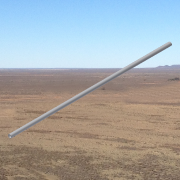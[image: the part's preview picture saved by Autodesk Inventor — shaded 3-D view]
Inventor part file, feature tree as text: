
AUTODESK INVENTOR PART (.ipt)
format: ipt  version: 2013 SP2 (Build 170200200, 200)  size: 123,392 bytes
history: native  units: in
note: dims shown in document units (in); Inventor stores cm internally (conversion verified against a paired STEP export)
features: extrude x1, sketch x1
ambient origin geometry x8: Origin, YZ Plane, XZ Plane, XY Plane, X Axis, Y Axis, Z Axis, Center Point
bodies: Solid1 (feature_tree)
feature tree (2):
  extrude  "Extrusion1"  Depth=23.0in TaperAngle=0.0deg
  sketch  "Sketch1"  dims[d0=0.5in d2=23.0in d3=0.0in]
